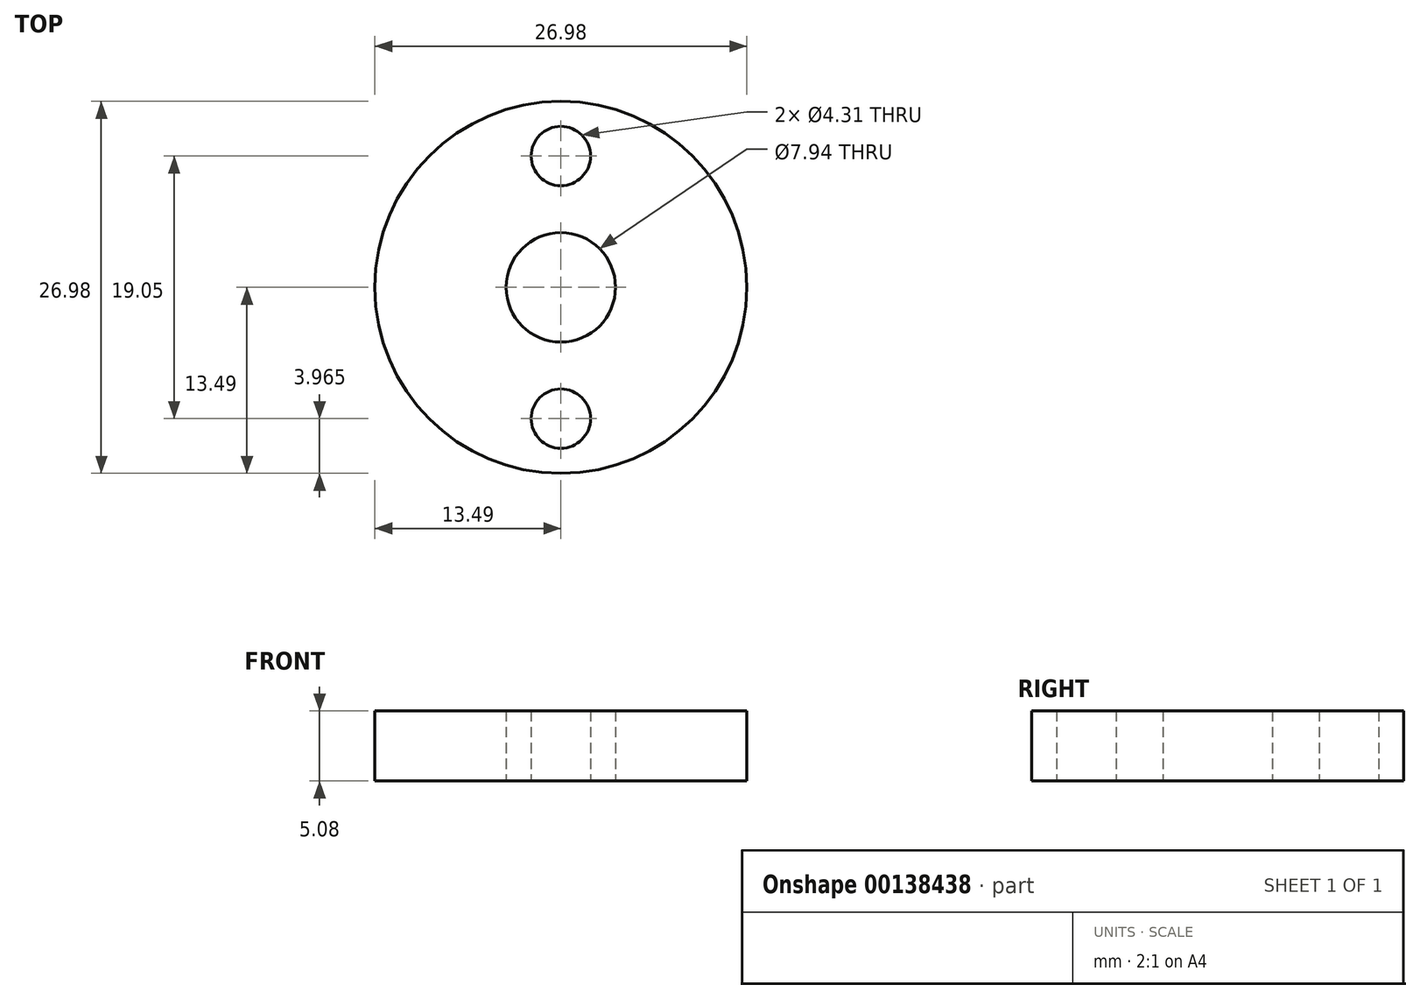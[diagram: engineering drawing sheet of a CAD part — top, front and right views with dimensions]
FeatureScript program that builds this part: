
annotation { "Feature Type Name" : "Feature", "Feature Type Description" : "" }
export const myFeature = defineFeature(function(context is Context, id is Id, definition is map)
    precondition{}
    {
        {
            var Q0;
            Q0=qCreatedBy(makeId("Top.planeOp"),FACE);
            var sketch = newSketch(context, id + "F0", { "sketchPlane" : qUnion([Q0])});
            skCircle(sketch, "E0", {"center": v(0, 0) * mm, "radius": 13.5 * mm});
            skLineSegment(sketch, "E1", {"start": v(0, 9.53) * mm, "end": v(0, -9.53) * mm, "construction": true});
            skCircle(sketch, "E2", {"center": v(0, -9.53) * mm, "radius": 3.97 * mm, "construction": true});
            skCircle(sketch, "E3", {"center": v(0, 0) * mm, "radius": 3.97 * mm});
            skCircle(sketch, "E4", {"center": v(0, 9.53) * mm, "radius": 2.15 * mm});
            skCircle(sketch, "E5", {"center": v(0, -9.53) * mm, "radius": 2.15 * mm});
            skSolve(sketch);
        }
        {
            var Q0;
            Q0 = qSketchRegion(id + "F0", true);
            extrude(context, id + "F1", {"entities" : qUnion([Q0]), "depth" : 5.08 * mm});
        }
    });
